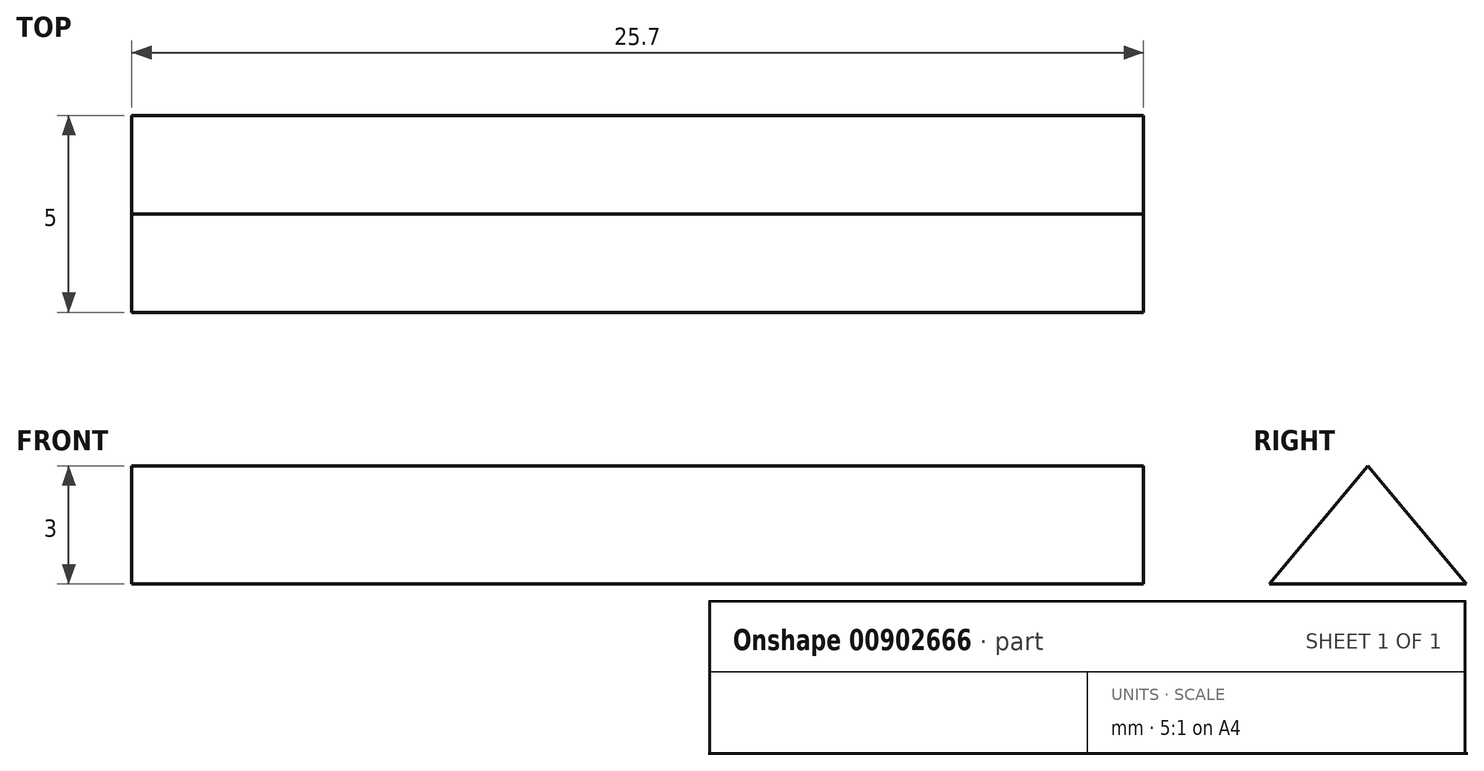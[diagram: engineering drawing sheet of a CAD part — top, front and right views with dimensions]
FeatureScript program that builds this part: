
annotation { "Feature Type Name" : "Feature", "Feature Type Description" : "" }
export const myFeature = defineFeature(function(context is Context, id is Id, definition is map)
    precondition{}
    {
        {
            var Q0;
            Q0=qCreatedBy(makeId("Right.planeOp"),FACE);
            var sketch = newSketch(context, id + "F0", { "sketchPlane" : qUnion([Q0])});
            skLineSegment(sketch, "E0", {"start": v(0, 0) * mm, "end": v(5, 0) * mm});
            skLineSegment(sketch, "E1", {"start": v(5, 0) * mm, "end": v(2.5, 3) * mm});
            skPoint(sketch, "E1.endSnap0", {"position": v(2.5, 0) * mm});
            skLineSegment(sketch, "E2", {"start": v(2.5, 3) * mm, "end": v(0, 0) * mm});
            skSolve(sketch);
        }
        {
            var Q0;
            Q0=makeQuery(id+"F0.imprint","IMPRINT",FACE,{"disambiguationData":[TD([[makeQuery(id+"F0.imprint","IMPRINT",EDGE,{"derivedFrom":sQuery(id+"F0.wireOp",EDGE,"E0")}),1.0]])]});
            extrude(context, id + "F1", {"entities" : qUnion([Q0]), "depth" : 25.7 * mm, "offsetDistance" : 25 * mm});
        }
    });
